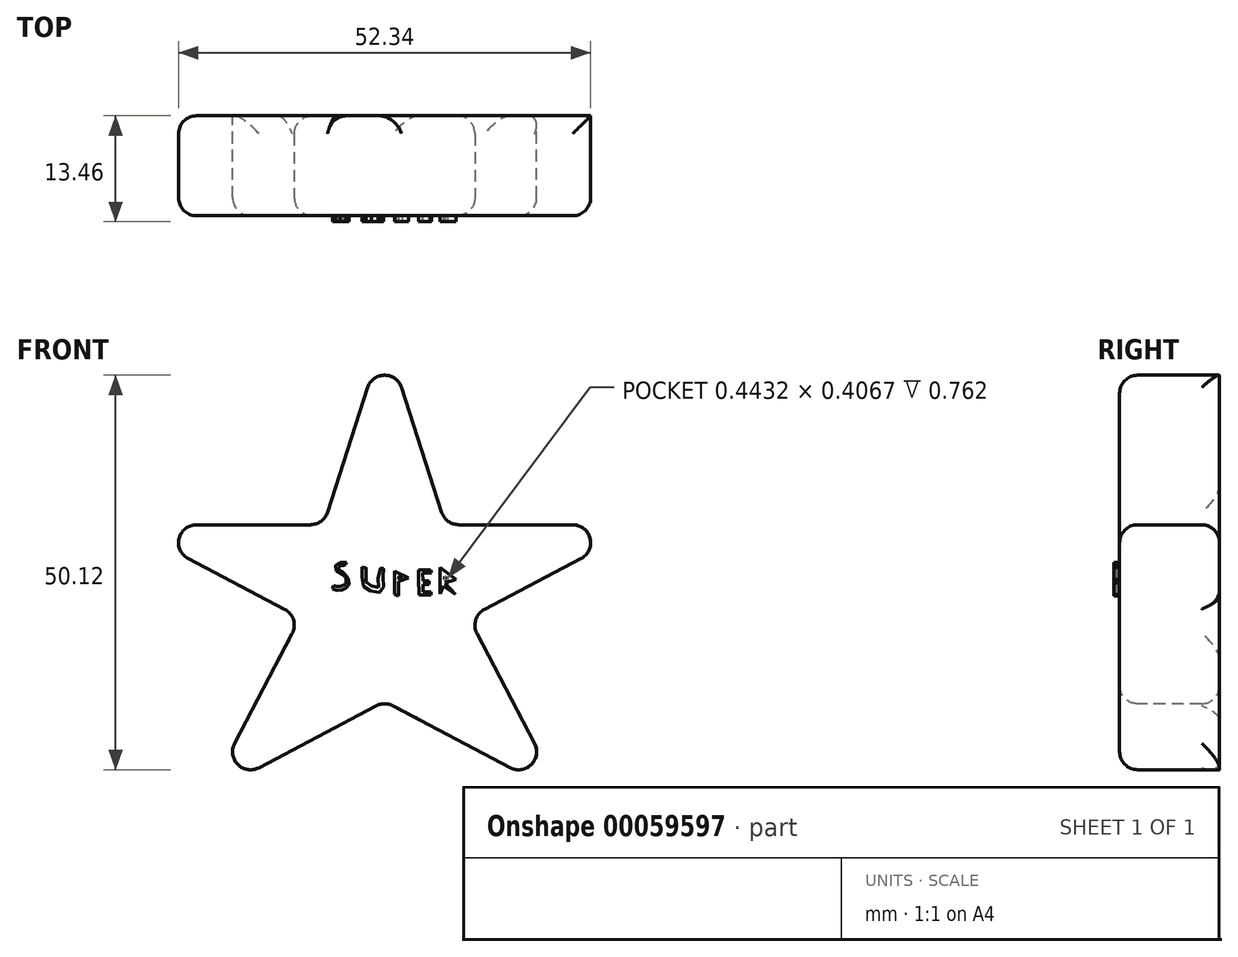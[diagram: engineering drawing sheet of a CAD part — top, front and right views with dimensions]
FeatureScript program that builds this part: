
annotation { "Feature Type Name" : "Feature", "Feature Type Description" : "" }
export const myFeature = defineFeature(function(context is Context, id is Id, definition is map)
    precondition{}
    {
        {
            var Q0;
            Q0=qCreatedBy(makeId("Front.planeOp"),FACE);
            var sketch = newSketch(context, id + "F0", { "sketchPlane" : qUnion([Q0])});
            skLineSegment(sketch, "E0", {"start": v(0, 35.98) * mm, "end": v(-7.77, 11.8) * mm});
            skLineSegment(sketch, "E1", {"start": v(-7.77, 11.8) * mm, "end": v(-33.17, 11.8) * mm});
            skLineSegment(sketch, "E2", {"start": v(-33.17, 11.8) * mm, "end": v(-10.67, 0) * mm});
            skLineSegment(sketch, "E3", {"start": v(-10.67, 0) * mm, "end": v(-22.47, -22.5) * mm});
            skLineSegment(sketch, "E4", {"start": v(-22.47, -22.5) * mm, "end": v(0, -10.65) * mm});
            skLineSegment(sketch, "E5", {"start": v(0, -10.65) * mm, "end": v(0, 35.98) * mm});
            skSolve(sketch);
        }
        {
            var Q0;
            Q0=makeQuery(id+"F0.imprint","IMPRINT",FACE,{"disambiguationData":[TD([[makeQuery(id+"F0.imprint","IMPRINT",EDGE,{"derivedFrom":sQuery(id+"F0.wireOp",EDGE,"E0")}),1.0]])]});
            var sketch = newSketch(context, id + "F1", { "sketchPlane" : qUnion([Q0])});
            skSolve(sketch);
        }
        {
            var Q0;
            Q0=makeQuery(id+"F1.imprint","IMPRINT",FACE,{"disambiguationData":[TD([[makeQuery(id+"F1.imprint","IMPRINT",EDGE,{"derivedFrom":makeQuery(id+"F0.imprint","IMPRINT",EDGE,{"derivedFrom":sQuery(id+"F0.wireOp",EDGE,"E0")})}),1.0]])]});
            extrude(context, id + "F2", {"entities" : qUnion([Q0]), "endBound" : BoundingType.SYMMETRIC, "depth" : 12.7 * mm});
        }
        {
            var Q0;
            Q0=makeQuery(id+"F2.opExtrude","SWEPT_BODY",BODY,{"disambiguationData":[OSD([sQuery(id+"F0.wireOp",EDGE,"E0"),sQuery(id+"F0.wireOp",EDGE,"E1"),sQuery(id+"F0.wireOp",EDGE,"E2"),sQuery(id+"F0.wireOp",EDGE,"E3"),sQuery(id+"F0.wireOp",EDGE,"E4"),sQuery(id+"F0.wireOp",EDGE,"E5")])]});
            var Q1;
            Q1=qCreatedBy(makeId("Right.planeOp"),FACE);
            mirror(context, id + "F3", {"operationType" : NewBodyOperationType.ADD, "entities" : qUnion([Q0]), "mirrorPlane" : qUnion([Q1])});
        }
        {
            var Q0;
            {var subQ0=makeQuery(id+"F2.opExtrude","CAP_FACE",FACE,{"disambiguationData":[OSD([sQuery(id+"F0.wireOp",EDGE,"E0"),sQuery(id+"F0.wireOp",EDGE,"E1"),sQuery(id+"F0.wireOp",EDGE,"E2"),sQuery(id+"F0.wireOp",EDGE,"E3"),sQuery(id+"F0.wireOp",EDGE,"E4"),sQuery(id+"F0.wireOp",EDGE,"E5")])],"isStart":false});Q0=makeQuery(id+"F3.boolean.opBoolean","MERGE",FACE,{"derivedFrom":[subQ0,makeQuery(id+"F3.opPattern","COPY",FACE,{"derivedFrom":subQ0,"instanceName":"1"})]});}
            var Q1;
            Q1=makeQuery(id+"F3.opPattern","COPY",FACE,{"derivedFrom":makeQuery(id+"F2.opExtrude","SWEPT_FACE",FACE,{"disambiguationData":[OSD([sQuery(id+"F0.wireOp",EDGE,"E0")])]}),"instanceName":"1"});
            var Q2;
            Q2=makeQuery(id+"F3.opPattern","COPY",FACE,{"derivedFrom":makeQuery(id+"F2.opExtrude","SWEPT_FACE",FACE,{"disambiguationData":[OSD([sQuery(id+"F0.wireOp",EDGE,"E1")])]}),"instanceName":"1"});
            var Q3;
            Q3=makeQuery(id+"F3.opPattern","COPY",FACE,{"derivedFrom":makeQuery(id+"F2.opExtrude","SWEPT_FACE",FACE,{"disambiguationData":[OSD([sQuery(id+"F0.wireOp",EDGE,"E3")])]}),"instanceName":"1"});
            var Q4;
            Q4=makeQuery(id+"F2.opExtrude","SWEPT_FACE",FACE,{"disambiguationData":[OSD([sQuery(id+"F0.wireOp",EDGE,"E4")])]});
            var Q5;
            Q5=makeQuery(id+"F2.opExtrude","SWEPT_FACE",FACE,{"disambiguationData":[OSD([sQuery(id+"F0.wireOp",EDGE,"E2")])]});
            var Q6;
            Q6=makeQuery(id+"F2.opExtrude","SWEPT_FACE",FACE,{"disambiguationData":[OSD([sQuery(id+"F0.wireOp",EDGE,"E1")])]});
            fillet(context, id + "F4", {"entities" : qUnion([Q0, Q1, Q2, Q3, Q4, Q5, Q6]), "radius" : 2.3 * mm, "tangentPropagation" : true, "allowEdgeOverflow" : false});
        }
        {
            var Q0;
            {var subQ0=makeQuery(id+"F2.opExtrude","CAP_FACE",FACE,{"disambiguationData":[OSD([sQuery(id+"F0.wireOp",EDGE,"E0"),sQuery(id+"F0.wireOp",EDGE,"E1"),sQuery(id+"F0.wireOp",EDGE,"E2"),sQuery(id+"F0.wireOp",EDGE,"E3"),sQuery(id+"F0.wireOp",EDGE,"E4"),sQuery(id+"F0.wireOp",EDGE,"E5")])],"isStart":false});Q0=makeQuery(id+"F3.boolean.opBoolean","MERGE",FACE,{"derivedFrom":[subQ0,makeQuery(id+"F3.opPattern","COPY",FACE,{"derivedFrom":subQ0,"instanceName":"1"})]});}
            var sketch = newSketch(context, id + "F8", { "sketchPlane" : qUnion([Q0])});
            skLineSegment(sketch, "E6", {"start": v(-4.88, 6.99) * mm, "end": v(-5.66, 6.99) * mm});
            skLineSegment(sketch, "E7", {"start": v(-5.66, 6.99) * mm, "end": v(-6.25, 6.62) * mm});
            skLineSegment(sketch, "E8", {"start": v(-6.25, 6.62) * mm, "end": v(-6.14, 6) * mm});
            skLineSegment(sketch, "E9", {"start": v(-6.14, 6) * mm, "end": v(-5.35, 5.5) * mm});
            skLineSegment(sketch, "E10", {"start": v(-5.35, 5.5) * mm, "end": v(-4.9, 5.04) * mm});
            skLineSegment(sketch, "E11", {"start": v(-4.9, 5.04) * mm, "end": v(-4.9, 4.3) * mm});
            skLineSegment(sketch, "E12", {"start": v(-4.9, 4.3) * mm, "end": v(-5.6, 3.93) * mm});
            skLineSegment(sketch, "E13", {"start": v(-5.6, 3.93) * mm, "end": v(-6.13, 3.93) * mm});
            skLineSegment(sketch, "E14", {"start": v(-6.13, 3.93) * mm, "end": v(-6.46, 4.07) * mm});
            skLineSegment(sketch, "E15", {"start": v(-6.46, 4.07) * mm, "end": v(-6.64, 3.63) * mm});
            skLineSegment(sketch, "E16", {"start": v(-6.64, 3.63) * mm, "end": v(-6.02, 3.44) * mm});
            skLineSegment(sketch, "E17", {"start": v(-6.02, 3.44) * mm, "end": v(-5.4, 3.5) * mm});
            skLineSegment(sketch, "E18", {"start": v(-5.4, 3.5) * mm, "end": v(-4.87, 3.76) * mm});
            skLineSegment(sketch, "E19", {"start": v(-4.87, 3.76) * mm, "end": v(-4.54, 4.18) * mm});
            skLineSegment(sketch, "E20", {"start": v(-4.54, 4.18) * mm, "end": v(-4.58, 4.77) * mm});
            skLineSegment(sketch, "E21", {"start": v(-4.58, 4.77) * mm, "end": v(-4.87, 5.37) * mm});
            skLineSegment(sketch, "E22", {"start": v(-4.87, 5.37) * mm, "end": v(-5.3, 5.78) * mm});
            skLineSegment(sketch, "E23", {"start": v(-5.3, 5.78) * mm, "end": v(-5.76, 6.08) * mm});
            skLineSegment(sketch, "E24", {"start": v(-5.76, 6.08) * mm, "end": v(-5.9, 6.43) * mm});
            skLineSegment(sketch, "E25", {"start": v(-5.9, 6.43) * mm, "end": v(-5.55, 6.64) * mm});
            skLineSegment(sketch, "E26", {"start": v(-5.55, 6.64) * mm, "end": v(-5.22, 6.64) * mm});
            skLineSegment(sketch, "E27", {"start": v(-5.22, 6.64) * mm, "end": v(-4.95, 6.76) * mm});
            skLineSegment(sketch, "E28", {"start": v(-4.95, 6.76) * mm, "end": v(-4.8, 6.97) * mm});
            skLineSegment(sketch, "E29", {"start": v(-4.8, 6.97) * mm, "end": v(-4.88, 6.99) * mm});
            skSolve(sketch);
        }
        {
            var Q0;
            Q0=makeQuery(id+"F8.imprint","IMPRINT",FACE,{"disambiguationData":[TD([[makeQuery(id+"F8.imprint","IMPRINT",EDGE,{"derivedFrom":sQuery(id+"F8.wireOp",EDGE,"E6")}),-1.0]])]});
            var sketch = newSketch(context, id + "F5", { "sketchPlane" : qUnion([Q0])});
            skSolve(sketch);
        }
        {
            var Q0;
            Q0=qSketchRegion(id+"F5",true);
            var Q1;
            Q1=makeQuery(id+"F8.imprint","IMPRINT",FACE,{"disambiguationData":[TD([[makeQuery(id+"F8.imprint","IMPRINT",EDGE,{"derivedFrom":sQuery(id+"F8.wireOp",EDGE,"E6")}),1.0]])]});
            extrude(context, id + "F9", {"entities" : qUnion([Q0, Q1]), "operationType" : NewBodyOperationType.ADD, "depth" : 0.76 * mm});
        }
        {
            var Q0;
            Q0=makeQuery(id+"F5.imprint","IMPRINT",FACE,{"disambiguationData":[TD([[makeQuery(id+"F5.imprint","IMPRINT",EDGE,{"derivedFrom":makeQuery(id+"F8.imprint","IMPRINT",EDGE,{"derivedFrom":sQuery(id+"F8.wireOp",EDGE,"E6")})}),-1.0]])]});
            var sketch = newSketch(context, id + "F6", { "sketchPlane" : qUnion([Q0])});
            skLineSegment(sketch, "E30", {"start": v(-2.85, 6.44) * mm, "end": v(-2.85, 5.14) * mm});
            skLineSegment(sketch, "E31", {"start": v(-2.85, 5.14) * mm, "end": v(-2.65, 3.98) * mm});
            skLineSegment(sketch, "E32", {"start": v(-2.65, 3.98) * mm, "end": v(-1.76, 3.4) * mm});
            skLineSegment(sketch, "E33", {"start": v(-1.76, 3.4) * mm, "end": v(-0.67, 3.18) * mm});
            skLineSegment(sketch, "E34", {"start": v(-0.67, 3.18) * mm, "end": v(-0.12, 3.91) * mm});
            skLineSegment(sketch, "E35", {"start": v(-0.12, 3.91) * mm, "end": v(-0.18, 5.14) * mm});
            skLineSegment(sketch, "E36", {"start": v(-0.18, 5.14) * mm, "end": v(-0.15, 6.22) * mm});
            skLineSegment(sketch, "E37", {"start": v(-0.15, 6.22) * mm, "end": v(-0.5, 6.3) * mm});
            skLineSegment(sketch, "E38", {"start": v(-0.5, 6.3) * mm, "end": v(-0.8, 5) * mm});
            skLineSegment(sketch, "E39", {"start": v(-0.8, 5) * mm, "end": v(-0.78, 3.85) * mm});
            skLineSegment(sketch, "E40", {"start": v(-0.78, 3.85) * mm, "end": v(-1.69, 4) * mm});
            skLineSegment(sketch, "E41", {"start": v(-1.69, 4) * mm, "end": v(-2.33, 4.5) * mm});
            skLineSegment(sketch, "E42", {"start": v(-2.33, 4.5) * mm, "end": v(-2.39, 5.59) * mm});
            skLineSegment(sketch, "E43", {"start": v(-2.39, 5.59) * mm, "end": v(-2.34, 6.35) * mm});
            skLineSegment(sketch, "E44", {"start": v(-2.34, 6.35) * mm, "end": v(-2.78, 6.31) * mm});
            skLineSegment(sketch, "E45", {"start": v(-2.78, 6.31) * mm, "end": v(-2.75, 6.37) * mm});
            skLineSegment(sketch, "E46", {"start": v(-2.75, 6.37) * mm, "end": v(-2.85, 6.44) * mm});
            skLineSegment(sketch, "E47", {"start": v(1.28, 5.93) * mm, "end": v(1.28, 2.91) * mm});
            skLineSegment(sketch, "E48", {"start": v(1.28, 2.91) * mm, "end": v(1.8, 2.78) * mm});
            skLineSegment(sketch, "E49", {"start": v(1.8, 2.78) * mm, "end": v(1.8, 4.6) * mm});
            skLineSegment(sketch, "E50", {"start": v(1.8, 4.6) * mm, "end": v(3.06, 5.02) * mm});
            skLineSegment(sketch, "E51", {"start": v(3.06, 5.02) * mm, "end": v(1.34, 5.86) * mm});
            skLineSegment(sketch, "E52", {"start": v(4.32, 6.03) * mm, "end": v(4.32, 4.95) * mm});
            skLineSegment(sketch, "E53", {"start": v(4.32, 4.95) * mm, "end": v(4.35, 2.89) * mm});
            skLineSegment(sketch, "E54", {"start": v(4.35, 2.89) * mm, "end": v(5.88, 2.9) * mm});
            skLineSegment(sketch, "E55", {"start": v(5.88, 2.9) * mm, "end": v(5.88, 3.26) * mm});
            skLineSegment(sketch, "E56", {"start": v(5.88, 3.26) * mm, "end": v(4.86, 3.27) * mm});
            skLineSegment(sketch, "E57", {"start": v(4.86, 3.27) * mm, "end": v(4.86, 4.24) * mm});
            skLineSegment(sketch, "E58", {"start": v(4.86, 4.24) * mm, "end": v(5.65, 4.22) * mm});
            skLineSegment(sketch, "E59", {"start": v(5.65, 4.22) * mm, "end": v(5.61, 4.67) * mm});
            skLineSegment(sketch, "E60", {"start": v(5.61, 4.67) * mm, "end": v(4.88, 4.67) * mm});
            skLineSegment(sketch, "E61", {"start": v(4.88, 4.67) * mm, "end": v(4.85, 5.66) * mm});
            skLineSegment(sketch, "E62", {"start": v(4.85, 5.66) * mm, "end": v(5.93, 5.64) * mm});
            skLineSegment(sketch, "E63", {"start": v(5.93, 5.64) * mm, "end": v(5.85, 6.07) * mm});
            skLineSegment(sketch, "E64", {"start": v(5.85, 6.07) * mm, "end": v(4.32, 6.03) * mm});
            skLineSegment(sketch, "E65", {"start": v(7.03, 2.97) * mm, "end": v(7.03, 6.34) * mm});
            skLineSegment(sketch, "E66", {"start": v(7.03, 6.34) * mm, "end": v(9.05, 4.84) * mm});
            skLineSegment(sketch, "E67", {"start": v(9.05, 4.84) * mm, "end": v(7.69, 4.4) * mm});
            skLineSegment(sketch, "E68", {"start": v(7.69, 4.4) * mm, "end": v(9, 2.94) * mm});
            skLineSegment(sketch, "E69", {"start": v(9, 2.94) * mm, "end": v(7.48, 4) * mm});
            skLineSegment(sketch, "E70", {"start": v(7.48, 4) * mm, "end": v(7.03, 2.97) * mm});
            skLineSegment(sketch, "E71", {"start": v(7.75, 4.84) * mm, "end": v(8.06, 4.94) * mm});
            skLineSegment(sketch, "E72", {"start": v(8.06, 4.94) * mm, "end": v(7.62, 5.24) * mm});
            skLineSegment(sketch, "E73", {"start": v(7.62, 5.24) * mm, "end": v(7.62, 4.84) * mm});
            skLineSegment(sketch, "E74", {"start": v(7.62, 4.84) * mm, "end": v(7.75, 4.84) * mm});
            skLineSegment(sketch, "E75", {"start": v(1.34, 5.86) * mm, "end": v(1.28, 5.93) * mm});
            skLineSegment(sketch, "E76", {"start": v(1.76, 4.9) * mm, "end": v(2.28, 5.14) * mm});
            skLineSegment(sketch, "E77", {"start": v(2.28, 5.14) * mm, "end": v(1.82, 5.3) * mm});
            skLineSegment(sketch, "E78", {"start": v(1.82, 5.3) * mm, "end": v(1.76, 4.9) * mm});
            skSolve(sketch);
        }
        {
            var Q0;
            Q0=qSketchRegion(id+"F6",true);
            extrude(context, id + "F7", {"entities" : qUnion([Q0]), "operationType" : NewBodyOperationType.ADD, "depth" : 0.76 * mm});
        }
    });
